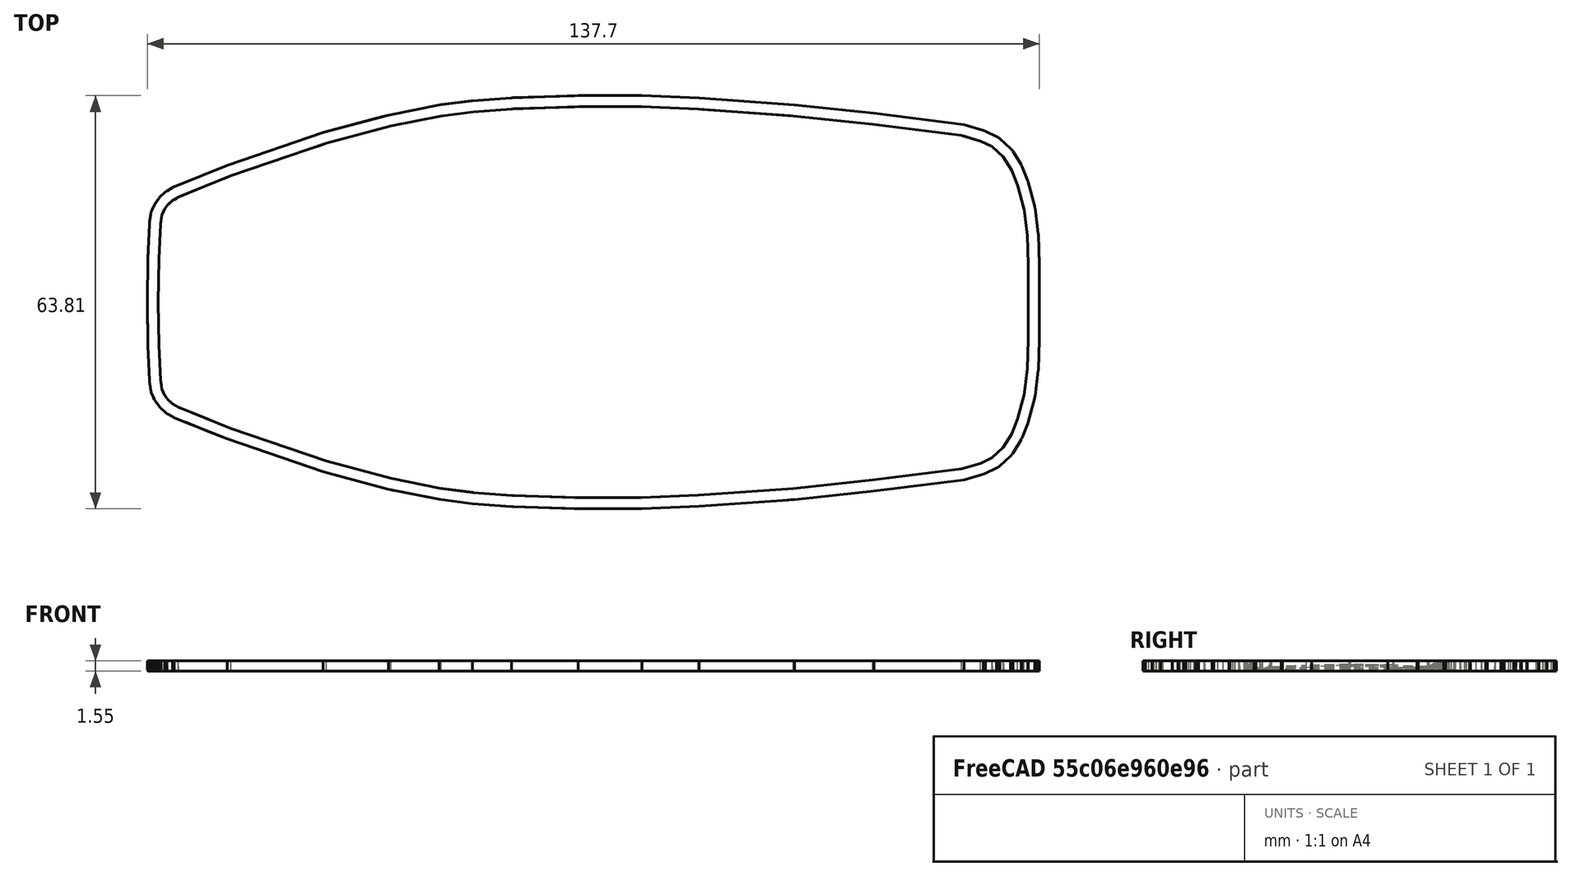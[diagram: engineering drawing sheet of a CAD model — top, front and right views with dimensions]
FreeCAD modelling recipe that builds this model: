
FCSTD DOCUMENT  (FreeCAD 1.0R39109 (Git))
Label: antenna_iunday
License: All rights reserved
LicenseURL: http://en.wikipedia.org/wiki/All_rights_reserved
objects: Part::Feature×4, Mesh::Feature×2, Part::Scale×2, Part::Box×1, Part::Cut×1, Part::MultiFuse×1
note: 9 computed .brp shape members not serialized (recipe doc carries the construction recipe); baked Part::Feature solids carry a one-line shape summary decoded from their .brp

FEATURE [Mesh::Feature] Antenna_cover_top_Kia_Rio_2017
FEATURE [Part::Feature] Antenna_cover_top_Kia_Rio_2018
  shape: large baked B-rep (58 MB .brp); summary skipped
FEATURE [Part::Feature] Antenna_cover_top_Kia_Rio_2019
  shape: large baked B-rep (58 MB .brp); summary skipped
FEATURE [Part::Box] Box  label="Cube"
  AttacherType = Attacher::AttachEngine3D
  Height = 300
  Length = 300
  Placement = pos=(2030,-7,98) rot=(0,0,1;0rad)
  Width = 300
FEATURE [Part::Cut] Cut
  Base = -> Antenna_cover_top_Kia_Rio_2019
  Placement = pos=(0,0,1.5) rot=(0,0,1;0rad)
  Tool = -> Box
FEATURE [Part::MultiFuse] Fusion
  Shapes = -> [Antenna_cover_top_Kia_Rio_2018,Cut]
FEATURE [Part::Feature] Cut001
  Placement = pos=(0,0,1.5) rot=(0,0,1;0rad)
  shape: bbox 140.5 x 65.12 x 1.585 mm, 1889 faces, 0 solids (baked)
FEATURE [Part::Scale] Scale
  Base = -> Cut001
  Placement = pos=(44.5,0.5,11) rot=(0,0,1;0rad)
  Uniform = true
  UniformScale = 0.98
  XScale = 1
  YScale = 1
  ZScale = 1
FEATURE [Part::Scale] Scale001
  Base = -> Cut001
  Uniform = true
  UniformScale = 0.95
  XScale = 1
  YScale = 1
  ZScale = 1
FEATURE [Part::Feature] Scale_solid  label="Scale (Solid)"
  shape: bbox 137.7 x 63.81 x 1.553 mm, 1889 faces (baked)
FEATURE [Mesh::Feature] Mesh  label="Fusion (Meshed)"
